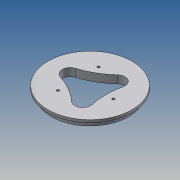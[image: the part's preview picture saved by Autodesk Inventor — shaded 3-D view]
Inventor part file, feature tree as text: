
AUTODESK INVENTOR PART (.ipt)
format: ipt  version: 2017 (Build 210142000, 142)  size: 176,640 bytes
history: native  units: mm
features: other x5, extrude x3, sketch x3, reference x1, projected_geometry x1
ambient origin geometry x8: Origin, YZ Plane, XZ Plane, XY Plane, X Axis, Y Axis, Z Axis, Center Point
bodies: Body1 (feature_tree), Body2 (feature_tree), Body3 (feature_tree)
feature tree (13):
  other  "Sólido1"
  extrude  "Extrusión1"  Depth=6.0mm TaperAngle=0.0deg
  extrude  "Extrusión2"  Depth=3.0mm TaperAngle=0.0deg
  extrude  "Extrusión3"  Depth=3.0mm TaperAngle=0.0deg
  sketch  "Boceto1"  dims[d0=88.0mm d1=6.0mm d2=0.0mm]
  reference  "Referencia1"
  sketch  "Boceto2"  dims[d3=4.0mm d4=3.0mm d5=0.0mm]
  projected_geometry  "Contorno proyectado1"
  other  "Sólido2"
  sketch  "Boceto3"  dims[d6=5.5mm d7=3.0mm d8=0.0mm]
  other  "Sólido3"
  other  "conjunto polea plato-carrete.iam"
  other  "Carrete Impreso:1"
